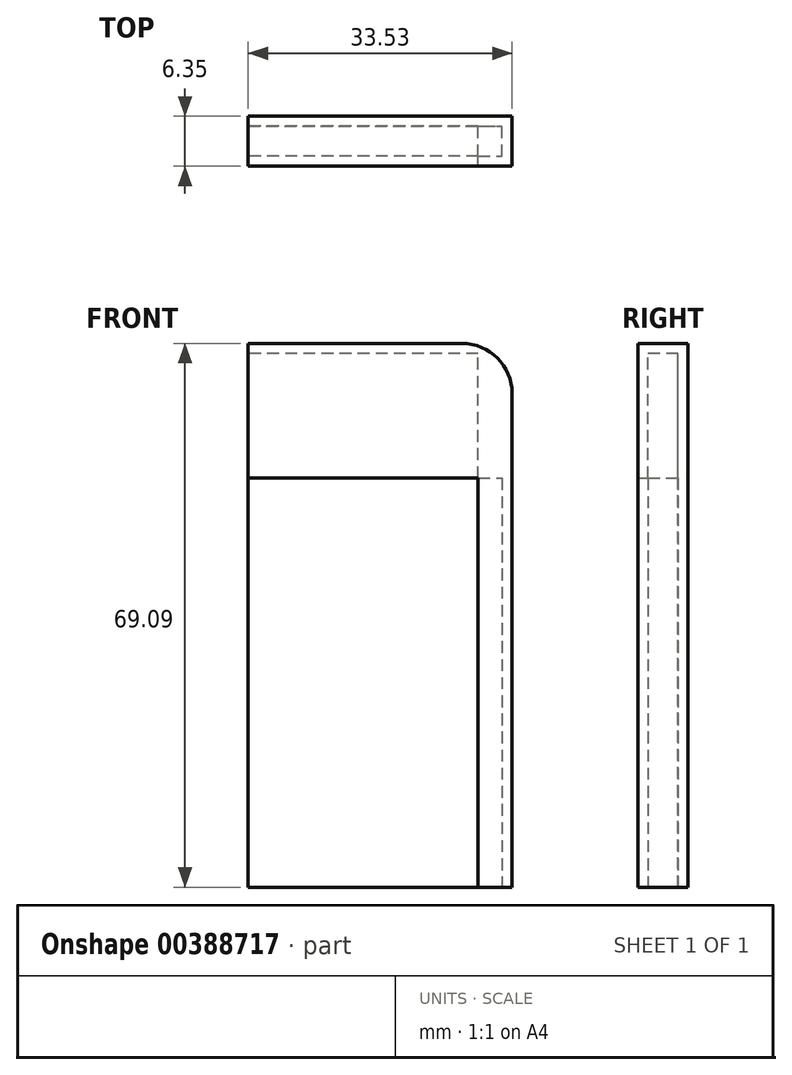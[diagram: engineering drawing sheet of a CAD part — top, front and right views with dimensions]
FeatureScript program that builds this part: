
annotation { "Feature Type Name" : "Feature", "Feature Type Description" : "" }
export const myFeature = defineFeature(function(context is Context, id is Id, definition is map)
    precondition{}
    {
        {
            var Q0;
            Q0=qCreatedBy(makeId("Front.planeOp"),FACE);
            var sketch = newSketch(context, id + "F0", { "sketchPlane" : qUnion([Q0])});
            skLineSegment(sketch, "E0.bottom", {"start": v(-39.03, -58.02) * mm, "end": v(33.53, -58.02) * mm});
            skLineSegment(sketch, "E0.top", {"start": v(0, 69.09) * mm, "end": v(27.18, 69.09) * mm});
            skLineSegment(sketch, "E0.right", {"start": v(33.53, 0) * mm, "end": v(33.53, 62.74) * mm});
            skLineSegment(sketch, "E1", {"start": v(0, 69.09) * mm, "end": v(0, 51.97) * mm});
            skLineSegment(sketch, "E2", {"start": v(29.22, 0) * mm, "end": v(33.53, 0) * mm});
            skLineSegment(sketch, "E3", {"start": v(0, 51.97) * mm, "end": v(29.22, 51.97) * mm});
            skLineSegment(sketch, "E4", {"start": v(29.22, 51.97) * mm, "end": v(29.22, 0) * mm});
            skPoint(sketch, "E5.visualSharp", {"position": v(33.53, 69.09) * mm});
            skArc(sketch, "E5.filletArc", {"start": v(33.53, 62.74) * mm, "mid": v(31.67, 67.23) * mm, "end": v(27.18, 69.09) * mm});
            skSolve(sketch);
        }
        {
            var Q0;
            Q0 = qSketchRegion(id + "F0", true);
            extrude(context, id + "F1", {"entities" : qUnion([Q0]), "depth" : 6.35 * mm});
        }
        {
            var Q0;
            Q0=makeQuery(id+"F1.opExtrude","SWEPT_FACE",FACE,{"disambiguationData":[OSD([sQuery(id+"F0.wireOp",EDGE,"E1")])]});
            var sketch = newSketch(context, id + "F2", { "sketchPlane" : qUnion([Q0])});
            skLineSegment(sketch, "E6.bottom", {"start": v(1.27, 51.97) * mm, "end": v(5.08, 51.97) * mm});
            skLineSegment(sketch, "E6.top", {"start": v(1.27, 67.82) * mm, "end": v(5.08, 67.82) * mm});
            skLineSegment(sketch, "E6.left", {"start": v(1.27, 51.97) * mm, "end": v(1.27, 67.82) * mm});
            skLineSegment(sketch, "E6.right", {"start": v(5.08, 51.97) * mm, "end": v(5.08, 67.82) * mm});
            skSolve(sketch);
        }
        {
            var Q0;
            Q0 = qSketchRegion(id + "F2", true);
            extrude(context, id + "F3", {"entities" : qUnion([Q0]), "operationType" : NewBodyOperationType.REMOVE, "oppositeDirection" : true, "depth" : 29.22 * mm});
        }
        {
            var Q0;
            Q0=makeQuery(id+"F1.opExtrude","SWEPT_FACE",FACE,{"disambiguationData":[OSD([sQuery(id+"F0.wireOp",EDGE,"E2")])]});
            var sketch = newSketch(context, id + "F4", { "sketchPlane" : qUnion([Q0])});
            skLineSegment(sketch, "E7.bottom", {"start": v(29.22, 5.08) * mm, "end": v(32.26, 5.08) * mm});
            skLineSegment(sketch, "E7.top", {"start": v(29.22, 1.27) * mm, "end": v(32.26, 1.27) * mm});
            skLineSegment(sketch, "E7.left", {"start": v(29.22, 5.08) * mm, "end": v(29.22, 1.27) * mm});
            skLineSegment(sketch, "E7.right", {"start": v(32.26, 5.08) * mm, "end": v(32.26, 1.27) * mm});
            skSolve(sketch);
        }
        {
            var Q0;
            Q0 = qSketchRegion(id + "F4", true);
            extrude(context, id + "F5", {"entities" : qUnion([Q0]), "operationType" : NewBodyOperationType.REMOVE, "oppositeDirection" : true, "depth" : 51.97 * mm});
        }
        {
            var Q0;
            {var subQ0=sQuery(id+"F0.wireOp",EDGE,"E4");var subQ1=makeQuery(id+"F1.opExtrude","SWEPT_FACE",FACE,{"disambiguationData":[OSD([subQ0])]});var subQ2=sQuery(id+"F2.wireOp",EDGE,"E6.left");var subQ3=makeQuery(id+"F3.opExtrude","CAP_FACE",FACE,{"disambiguationData":[OSD([sQuery(id+"F2.wireOp",EDGE,"E6.bottom"),sQuery(id+"F2.wireOp",EDGE,"E6.top"),subQ2,sQuery(id+"F2.wireOp",EDGE,"E6.right")])],"isStart":false});var subQ4=sQuery(id+"F0.wireOp",EDGE,"E2");var subQ6=sQuery(id+"F0.wireOp",EDGE,"E3");Q0=makeQuery(id+"F5.boolean.opBoolean","SPLIT",FACE,{"disambiguationData":[TD([makeQuery(id+"F1.opExtrude","CAP_FACE",FACE,{"disambiguationData":[OSD([sQuery(id+"F0.wireOp",EDGE,"E0.top"),sQuery(id+"F0.wireOp",EDGE,"E0.right"),sQuery(id+"F0.wireOp",EDGE,"E1"),subQ4,subQ6,subQ0,sQuery(id+"F0.wireOp",EDGE,"E5.filletArc")])],"isStart":true})])],"derivedFrom":makeQuery(id+"F3.boolean.opBoolean","MERGE",FACE,{"derivedFrom":[subQ1,subQ3]})});}
            var sketch = newSketch(context, id + "F6", { "sketchPlane" : qUnion([Q0])});
            skLineSegment(sketch, "E8.bottom", {"start": v(0, 51.97) * mm, "end": v(1.27, 51.97) * mm});
            skLineSegment(sketch, "E8.top", {"start": v(0, 0) * mm, "end": v(1.27, 0) * mm});
            skLineSegment(sketch, "E8.left", {"start": v(0, 51.97) * mm, "end": v(0, 0) * mm});
            skLineSegment(sketch, "E8.right", {"start": v(1.27, 51.97) * mm, "end": v(1.27, 0) * mm});
            skSolve(sketch);
        }
        {
            var Q0;
            Q0 = qSketchRegion(id + "F6", true);
            var Q1;
            Q1=makeQuery(id+"F1.opExtrude","SWEPT_FACE",FACE,{"disambiguationData":[OSD([sQuery(id+"F0.wireOp",EDGE,"E1")])]});
            extrude(context, id + "F7", {"entities" : qUnion([Q0]), "operationType" : NewBodyOperationType.ADD, "endBound" : BoundingType.UP_TO_SURFACE, "endBoundEntityFace" : qUnion([Q1]), "depth" : 25.4 * mm});
        }
    });
